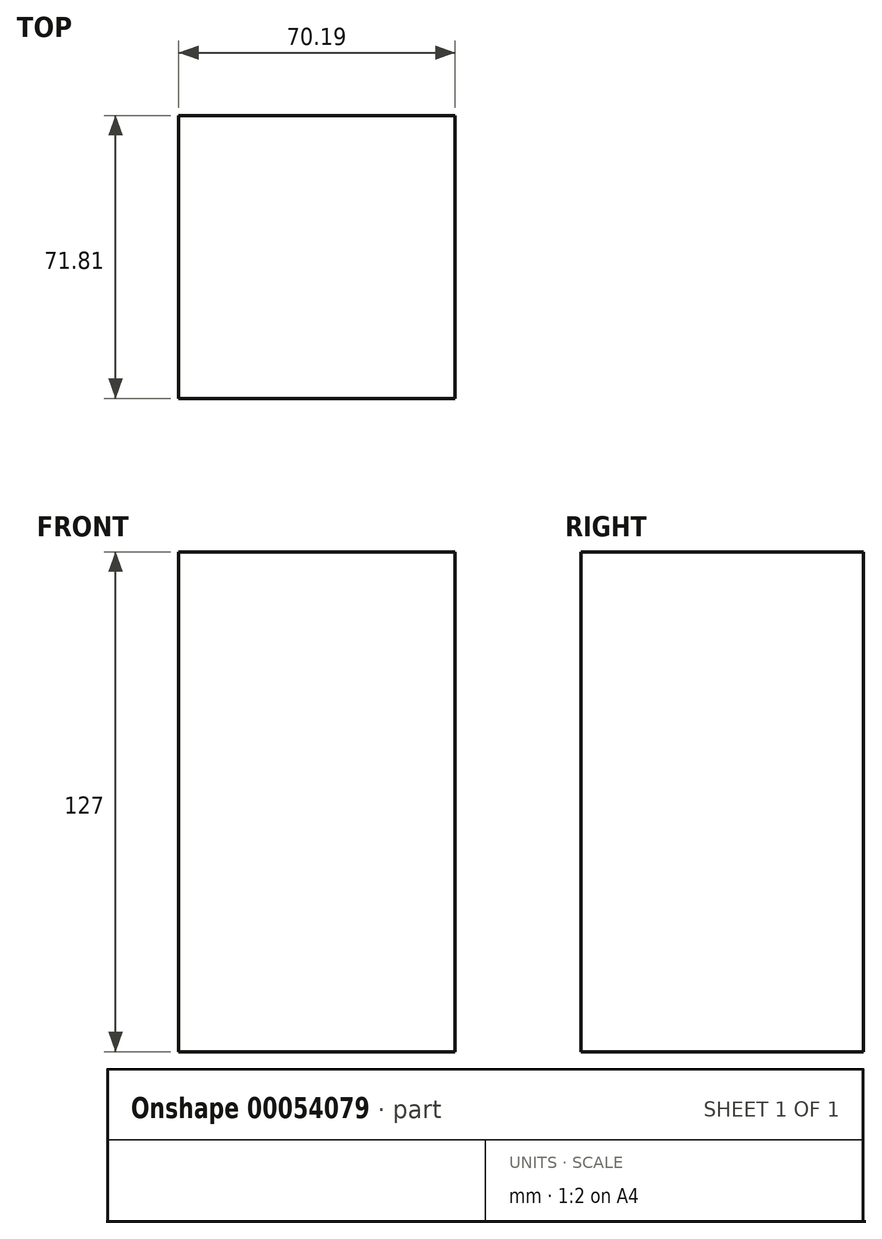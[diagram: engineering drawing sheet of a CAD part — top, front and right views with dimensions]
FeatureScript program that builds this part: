
annotation { "Feature Type Name" : "Feature", "Feature Type Description" : "" }
export const myFeature = defineFeature(function(context is Context, id is Id, definition is map)
    precondition{}
    {
        {
            var Q0;
            Q0=qCreatedBy(makeId("Top.planeOp"),FACE);
            var sketch = newSketch(context, id + "F0", { "sketchPlane" : qUnion([Q0])});
            skLineSegment(sketch, "E0.bottom", {"start": v(-74.58, 5.43) * mm, "end": v(-4.39, 5.43) * mm});
            skLineSegment(sketch, "E0.top", {"start": v(-74.58, 77.24) * mm, "end": v(-4.39, 77.24) * mm});
            skLineSegment(sketch, "E0.left", {"start": v(-74.58, 5.43) * mm, "end": v(-74.58, 77.24) * mm});
            skLineSegment(sketch, "E0.right", {"start": v(-4.39, 5.43) * mm, "end": v(-4.39, 77.24) * mm});
            skSolve(sketch);
        }
        {
            var Q0;
            Q0=makeQuery(id+"F0.imprint","IMPRINT",FACE,{"disambiguationData":[TD([[makeQuery(id+"F0.imprint","IMPRINT",EDGE,{"derivedFrom":sQuery(id+"F0.wireOp",EDGE,"E0.bottom")}),1.0]])]});
            extrude(context, id + "F1", {"entities" : qUnion([Q0]), "depth" : 127 * mm});
        }
        {
            var Q0;
            Q0=makeQuery(id+"F1.opExtrude","CAP_FACE",FACE,{"disambiguationData":[OSD([sQuery(id+"F0.wireOp",EDGE,"E0.bottom"),sQuery(id+"F0.wireOp",EDGE,"E0.top"),sQuery(id+"F0.wireOp",EDGE,"E0.left"),sQuery(id+"F0.wireOp",EDGE,"E0.right")])],"isStart":false});
            var sketch = newSketch(context, id + "F2", { "sketchPlane" : qUnion([Q0])});
            skSolve(sketch);
        }
        {
            var Q0;
            Q0=makeQuery(id+"F2.imprint","IMPRINT",FACE,{"disambiguationData":[TD([[makeQuery(id+"F2.imprint","IMPRINT",EDGE,{"derivedFrom":makeQuery(id+"F1.opExtrude","CAP_EDGE",EDGE,{"disambiguationData":[OSD([sQuery(id+"F0.wireOp",EDGE,"E0.bottom")])],"isStart":false})}),1.0]])]});
            var sketch = newSketch(context, id + "F3", { "sketchPlane" : qUnion([Q0])});
            skSolve(sketch);
        }
    });
